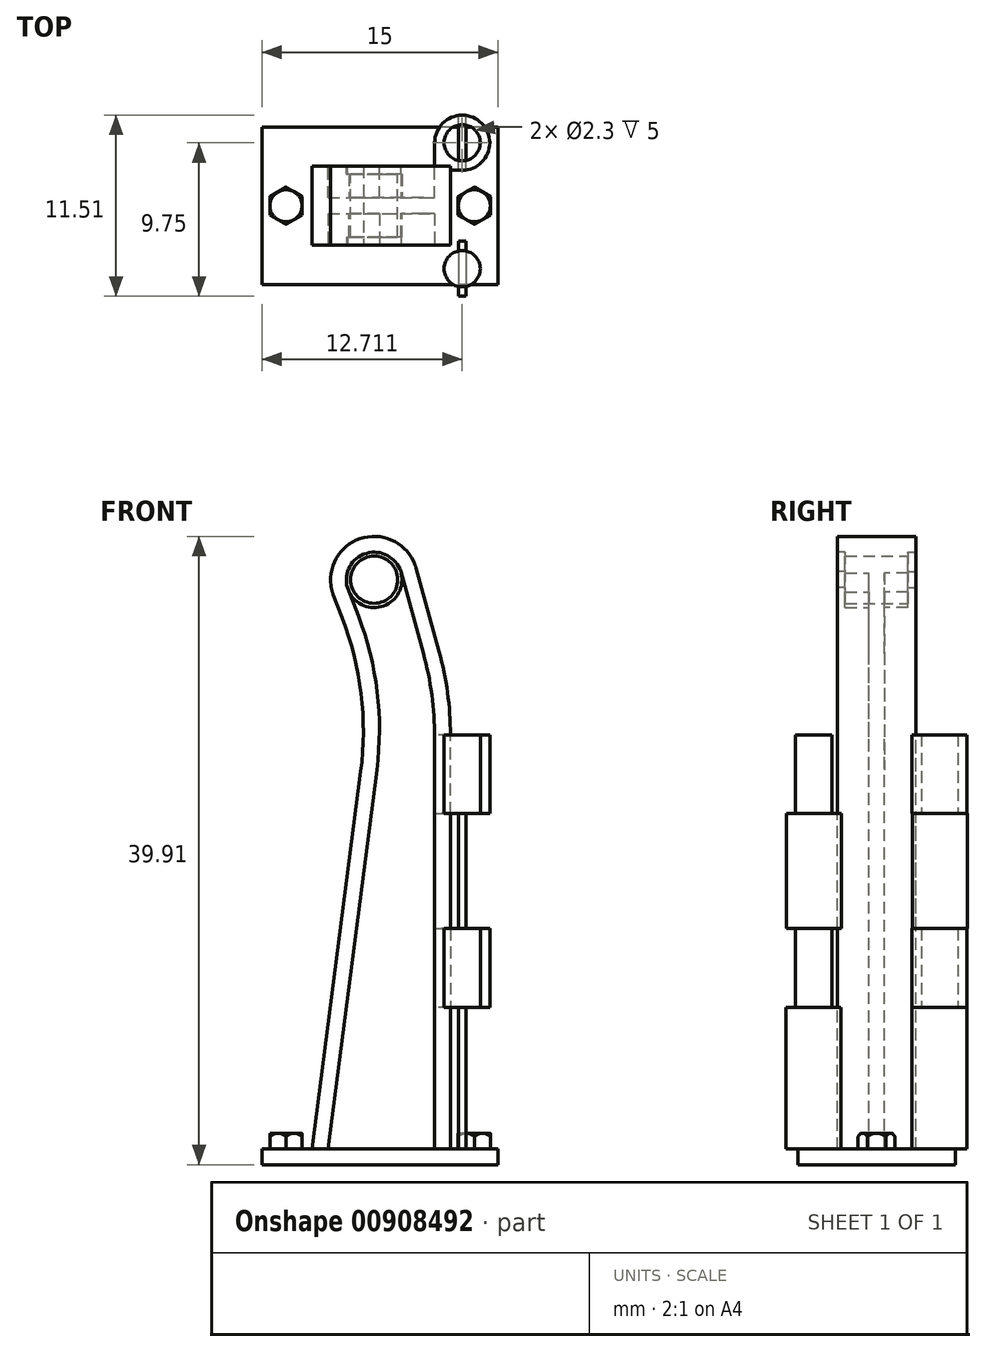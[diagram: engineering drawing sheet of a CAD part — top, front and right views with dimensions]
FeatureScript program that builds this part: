
annotation { "Feature Type Name" : "Feature", "Feature Type Description" : "" }
export const myFeature = defineFeature(function(context is Context, id is Id, definition is map)
    precondition{}
    {
        {
            var Q0;
            Q0=qCreatedBy(makeId("Front.planeOp"),FACE);
            var sketch = newSketch(context, id + "F0", { "sketchPlane" : qUnion([Q0])});
            skLineSegment(sketch, "E0.bottom", {"start": v(-10.54, 39.86) * mm, "end": v(4.46, 40) * mm, "construction": true});
            skLineSegment(sketch, "E0.left", {"start": v(-10.54, 39.86) * mm, "end": v(-10.54, 0) * mm, "construction": true});
            skLineSegment(sketch, "E0.right", {"start": v(4.46, 40) * mm, "end": v(4.46, 0) * mm, "construction": true});
            skLineSegment(sketch, "E1", {"start": v(4.46, 0) * mm, "end": v(4.46, 30) * mm});
            skLineSegment(sketch, "E2", {"start": v(-4.46, 0) * mm, "end": v(-0.58, 30) * mm});
            skLineSegment(sketch, "E3", {"start": v(-0.58, 30) * mm, "end": v(-3.03, 36.33) * mm});
            skLineSegment(sketch, "E4", {"start": v(4.46, 30) * mm, "end": v(2.27, 37.94) * mm});
            skArc(sketch, "E5", {"start": v(2.27, 37.94) * mm, "mid": v(-1.18, 39.79) * mm, "end": v(-3.03, 36.33) * mm});
            skLineSegment(sketch, "E6", {"start": v(-4.46, 0) * mm, "end": v(4.46, 0) * mm});
            skSolve(sketch);
        }
        {
            var Q0;
            Q0=makeQuery(id+"F0.imprint","IMPRINT",FACE,{"disambiguationData":[TD([[makeQuery(id+"F0.imprint","IMPRINT",EDGE,{"derivedFrom":sQuery(id+"F0.wireOp",EDGE,"E1")}),1.0]])]});
            extrude(context, id + "F1", {"entities" : qUnion([Q0]), "endBound" : BoundingType.SYMMETRIC, "depth" : 5 * mm, "offsetDistance" : 25 * mm});
        }
        {
            var Q0;
            Q0=makeQuery(id+"F1.opExtrude","SWEPT_EDGE",EDGE,{"disambiguationData":[OSD([sQuery(id+"F0.wireOp",EDGE,"E1"),sQuery(id+"F0.wireOp",EDGE,"E4")])]});
            var Q1;
            Q1=makeQuery(id+"F1.opExtrude","SWEPT_EDGE",EDGE,{"disambiguationData":[OSD([sQuery(id+"F0.wireOp",EDGE,"E2"),sQuery(id+"F0.wireOp",EDGE,"E3")])]});
            fillet(context, id + "F2", {"entities" : qUnion([Q0, Q1]), "radius" : 20 * mm, "tangentPropagation" : true, "allowEdgeOverflow" : false});
        }
        {
            var Q0;
            Q0=makeQuery(id+"F1.opExtrude","SWEPT_EDGE",EDGE,{"disambiguationData":[OSD([sQuery(id+"F0.wireOp",EDGE,"E3"),sQuery(id+"F0.wireOp",EDGE,"E5")])]});
            var Q1;
            {var subQ0=sQuery(id+"F0.wireOp",EDGE,"E3");Q1=makeQuery(id+"F2.opFillet","BLEND_EDGE",EDGE,{"blendedFrom":[makeQuery(id+"F1.opExtrude","SWEPT_EDGE",EDGE,{"disambiguationData":[OSD([sQuery(id+"F0.wireOp",EDGE,"E2"),subQ0])]}),makeQuery(id+"F1.opExtrude","SWEPT_FACE",FACE,{"disambiguationData":[OSD([subQ0])]})],"blendedInto":[makeQuery(id+"F1.opExtrude","SWEPT_FACE",FACE,{"disambiguationData":[OSD([subQ0])]})]});}
            var Q2;
            Q2=makeQuery(id+"F1.opExtrude","SWEPT_EDGE",EDGE,{"disambiguationData":[OSD([sQuery(id+"F0.wireOp",EDGE,"E4"),sQuery(id+"F0.wireOp",EDGE,"E5")])]});
            fillet(context, id + "F3", {"entities" : qUnion([Q0, Q1, Q2]), "radius" : 2.5 * mm, "tangentPropagation" : true, "allowEdgeOverflow" : false});
        }
        {
            var Q0;
            Q0=makeQuery(id+"F1.opExtrude","CAP_FACE",FACE,{"disambiguationData":[OSD([sQuery(id+"F0.wireOp",EDGE,"E1"),sQuery(id+"F0.wireOp",EDGE,"E2"),sQuery(id+"F0.wireOp",EDGE,"E3"),sQuery(id+"F0.wireOp",EDGE,"E4"),sQuery(id+"F0.wireOp",EDGE,"E5"),sQuery(id+"F0.wireOp",EDGE,"E6")])],"isStart":false});
            var sketch = newSketch(context, id + "F4", { "sketchPlane" : qUnion([Q0])});
            skLineSegment(sketch, "E7.0", {"start": v(3.46, 1) * mm, "end": v(3.46, 29.86) * mm});
            skArc(sketch, "E7.1", {"start": v(1.31, 37.66) * mm, "mid": v(-0.88, 38.83) * mm, "end": v(-2.08, 36.66) * mm});
            skLineSegment(sketch, "E7.2", {"start": v(0.44, 30.12) * mm, "end": v(-2.08, 36.66) * mm});
            skLineSegment(sketch, "E7.3", {"start": v(3.46, 29.86) * mm, "end": v(1.31, 37.66) * mm});
            skLineSegment(sketch, "E7.4", {"start": v(-3.32, 1) * mm, "end": v(0.44, 30.12) * mm});
            skLineSegment(sketch, "E7.5", {"start": v(-3.32, 1) * mm, "end": v(3.46, 1) * mm});
            skLineSegment(sketch, "E8", {"start": v(-0.38, 37.14) * mm, "end": v(-0.38, 38.32) * mm, "construction": true});
            skSolve(sketch);
        }
        {
            var Q0;
            Q0=makeQuery(id+"F4.imprint","IMPRINT",FACE,{"disambiguationData":[TD([[makeQuery(id+"F4.imprint","IMPRINT",EDGE,{"derivedFrom":sQuery(id+"F4.wireOp",EDGE,"E7.0")}),1.0]])]});
            extrude(context, id + "F5", {"entities" : qUnion([Q0]), "operationType" : NewBodyOperationType.REMOVE, "oppositeDirection" : true, "depth" : 2 * mm, "offsetDistance" : 25 * mm});
        }
        {
            var Q0;
            Q0=makeQuery(id+"F5.boolean.opBoolean","COPY",EDGE,{"derivedFrom":makeQuery(id+"F5.opExtrude","SWEPT_EDGE",EDGE,{"disambiguationData":[OSD([sQuery(id+"F4.wireOp",EDGE,"E7.2"),sQuery(id+"F4.wireOp",EDGE,"E7.4")])]})});
            var Q1;
            Q1=makeQuery(id+"F5.boolean.opBoolean","COPY",EDGE,{"derivedFrom":makeQuery(id+"F5.opExtrude","SWEPT_EDGE",EDGE,{"disambiguationData":[OSD([sQuery(id+"F4.wireOp",EDGE,"E7.0"),sQuery(id+"F4.wireOp",EDGE,"E7.3")])]})});
            fillet(context, id + "F6", {"entities" : qUnion([Q0, Q1]), "radius" : 20 * mm, "tangentPropagation" : true, "allowEdgeOverflow" : false});
        }
        {
            var Q0;
            Q0=makeQuery(id+"F1.opExtrude","CAP_FACE",FACE,{"disambiguationData":[OSD([sQuery(id+"F0.wireOp",EDGE,"E1"),sQuery(id+"F0.wireOp",EDGE,"E2"),sQuery(id+"F0.wireOp",EDGE,"E3"),sQuery(id+"F0.wireOp",EDGE,"E4"),sQuery(id+"F0.wireOp",EDGE,"E5"),sQuery(id+"F0.wireOp",EDGE,"E6")])],"isStart":true});
            var sketch = newSketch(context, id + "F7", { "sketchPlane" : qUnion([Q0])});
            skLineSegment(sketch, "E9.MirrorCS", {"start": v(-3.46, 1) * mm, "end": v(-3.46, 29.86) * mm});
            skLineSegment(sketch, "E10.MirrorCS", {"start": v(-3.46, 29.86) * mm, "end": v(-1.31, 37.66) * mm});
            skArc(sketch, "E11.MirrorCS", {"start": v(-1.31, 37.66) * mm, "mid": v(0.88, 38.83) * mm, "end": v(2.08, 36.66) * mm});
            skLineSegment(sketch, "E12.MirrorCS", {"start": v(3.32, 1) * mm, "end": v(-3.46, 1) * mm});
            skLineSegment(sketch, "E13.MirrorCS", {"start": v(3.32, 1) * mm, "end": v(-0.44, 30.12) * mm});
            skLineSegment(sketch, "E14.MirrorCS", {"start": v(-0.44, 30.12) * mm, "end": v(2.08, 36.66) * mm});
            skSolve(sketch);
        }
        {
            var Q0;
            Q0=makeQuery(id+"F7.imprint","IMPRINT",FACE,{"disambiguationData":[TD([[makeQuery(id+"F7.imprint","IMPRINT",EDGE,{"derivedFrom":sQuery(id+"F7.wireOp",EDGE,"E9.MirrorCS")}),-1.0]])]});
            extrude(context, id + "F8", {"entities" : qUnion([Q0]), "operationType" : NewBodyOperationType.REMOVE, "oppositeDirection" : true, "depth" : 2 * mm, "offsetDistance" : 25 * mm});
        }
        {
            var Q0;
            Q0=qCreatedBy(makeId("Top.planeOp"),FACE);
            var sketch = newSketch(context, id + "F9", { "sketchPlane" : qUnion([Q0])});
            skLineSegment(sketch, "E15.bottom", {"start": v(7.5, -5) * mm, "end": v(-7.5, -5) * mm});
            skLineSegment(sketch, "E15.top", {"start": v(7.5, 5) * mm, "end": v(-7.5, 5) * mm});
            skLineSegment(sketch, "E15.left", {"start": v(7.5, -5) * mm, "end": v(7.5, 5) * mm});
            skLineSegment(sketch, "E15.right", {"start": v(-7.5, -5) * mm, "end": v(-7.5, 5) * mm});
            skPoint(sketch, "E15.middle", {"position": v(0, 0) * mm});
            skLineSegment(sketch, "E16", {"start": v(-16.24, 0) * mm, "end": v(12.47, 0) * mm, "construction": true});
            skLineSegment(sketch, "E17", {"start": v(-5.98, 1.97) * mm, "end": v(-5.98, -1.97) * mm, "construction": true});
            skLineSegment(sketch, "E18.MirrorCS", {"start": v(5.98, 1.97) * mm, "end": v(5.98, -1.97) * mm, "construction": true});
            skPoint(sketch, "E19", {"position": v(-5.98, 0) * mm});
            skPoint(sketch, "E20", {"position": v(5.98, 0) * mm});
            skSolve(sketch);
        }
        {
            var Q0;
            Q0=makeQuery(id+"F9.imprint","IMPRINT",FACE,{"disambiguationData":[TD([[makeQuery(id+"F9.imprint","IMPRINT",EDGE,{"derivedFrom":sQuery(id+"F9.wireOp",EDGE,"E15.bottom")}),-1.0]])]});
            extrude(context, id + "F10", {"entities" : qUnion([Q0]), "operationType" : NewBodyOperationType.ADD, "depth" : 1 * mm, "offsetDistance" : 25 * mm});
        }
        {
            var Q0;
            Q0=qCreatedBy(makeId("Top.planeOp"),FACE);
            cPlane(context, id + "F11", {"entities" : qUnion([Q0]), "cplaneType" : CPlaneType.OFFSET, "offset" : 10 * mm, "width" : 150 * mm, "height" : 150 * mm});
        }
        {
            var Q0;
            Q0=makeQuery(id+"F8.boolean.opBoolean","COPY",EDGE,{"derivedFrom":makeQuery(id+"F8.opExtrude","SWEPT_EDGE",EDGE,{"disambiguationData":[OSD([sQuery(id+"F7.wireOp",EDGE,"E13.MirrorCS"),sQuery(id+"F7.wireOp",EDGE,"E14.MirrorCS")])]})});
            var Q1;
            Q1=makeQuery(id+"F8.boolean.opBoolean","COPY",EDGE,{"derivedFrom":makeQuery(id+"F8.opExtrude","SWEPT_EDGE",EDGE,{"disambiguationData":[OSD([sQuery(id+"F7.wireOp",EDGE,"E9.MirrorCS"),sQuery(id+"F7.wireOp",EDGE,"E10.MirrorCS")])]})});
            fillet(context, id + "F12", {"entities" : qUnion([Q0, Q1]), "radius" : 20 * mm, "tangentPropagation" : true, "allowEdgeOverflow" : false});
        }
        {
            var Q0;
            Q0=qCreatedBy(id+"F11.planeOp",FACE);
            var sketch = newSketch(context, id + "F13", { "sketchPlane" : qUnion([Q0])});
            skArc(sketch, "E21", {"start": v(5.21, 2.25) * mm, "mid": v(6.45, 5.24) * mm, "end": v(3.46, 4) * mm});
            skLineSegment(sketch, "E22", {"start": v(5.21, 2.5) * mm, "end": v(5.21, 5.48) * mm, "construction": true});
            skCircle(sketch, "E23", {"center": v(5.21, 4) * mm, "radius": 1.15 * mm});
            skLineSegment(sketch, "E24", {"start": v(3.46, 4) * mm, "end": v(3.46, 2.25) * mm});
            skLineSegment(sketch, "E25", {"start": v(3.46, 2.25) * mm, "end": v(5.21, 2.25) * mm});
            skCircle(sketch, "E26.MirrorC", {"center": v(5.21, -4) * mm, "radius": 1.15 * mm});
            skLineSegment(sketch, "E27.MirrorCS", {"start": v(5.21, -2.5) * mm, "end": v(5.21, -5.48) * mm, "construction": true});
            skLineSegment(sketch, "E28", {"start": v(6, -0.4) * mm, "end": v(8.23, -0.4) * mm, "construction": true});
            skPoint(sketch, "E29.orphan", {"position": v(3.46, 2.5) * mm});
            skLineSegment(sketch, "E30", {"start": v(5.96, 0) * mm, "end": v(10.84, 0) * mm, "construction": true});
            skArc(sketch, "E31.MirrorCS", {"start": v(5.21, -2.25) * mm, "mid": v(6.45, -5.24) * mm, "end": v(3.46, -4) * mm});
            skLineSegment(sketch, "E32.MirrorCS", {"start": v(3.46, -4) * mm, "end": v(3.46, -2.25) * mm});
            skLineSegment(sketch, "E33.MirrorCS", {"start": v(3.46, -2.25) * mm, "end": v(5.21, -2.25) * mm});
            skSolve(sketch);
        }
        {
            var Q0;
            Q0=makeQuery(id+"F13.imprint","IMPRINT",FACE,{"disambiguationData":[TD([[makeQuery(id+"F13.imprint","IMPRINT",EDGE,{"derivedFrom":sQuery(id+"F13.wireOp",EDGE,"E26.MirrorC")}),1.0]])]});
            var Q1;
            Q1=makeQuery(id+"F13.imprint","IMPRINT",FACE,{"disambiguationData":[TD([[makeQuery(id+"F13.imprint","IMPRINT",EDGE,{"derivedFrom":sQuery(id+"F13.wireOp",EDGE,"E21")}),1.0]])]});
            extrude(context, id + "F14", {"entities" : qUnion([Q0, Q1]), "operationType" : NewBodyOperationType.ADD, "depth" : 17.3 * mm, "offsetDistance" : 25 * mm});
        }
        {
            var Q0;
            Q0=qCreatedBy(makeId("Right.planeOp"),FACE);
            cPlane(context, id + "F15", {"entities" : qUnion([Q0]), "cplaneType" : CPlaneType.OFFSET, "offset" : 8 * mm, "width" : 150 * mm, "height" : 150 * mm});
        }
        {
            var Q0;
            Q0=qCreatedBy(id+"F15.planeOp",FACE);
            var sketch = newSketch(context, id + "F16", { "sketchPlane" : qUnion([Q0])});
            skLineSegment(sketch, "E34", {"start": v(-2.5, 32.3) * mm, "end": v(-2.5, 27.3) * mm, "construction": true});
            skLineSegment(sketch, "E35", {"start": v(-2.5, 5) * mm, "end": v(-2.5, 0) * mm, "construction": true});
            skLineSegment(sketch, "E36.top", {"start": v(-2.5, 5) * mm, "end": v(-6.5, 5) * mm, "construction": true});
            skLineSegment(sketch, "E36.left", {"start": v(-2.5, 10) * mm, "end": v(-2.5, 5) * mm, "construction": true});
            skLineSegment(sketch, "E36.right", {"start": v(-6.5, 10) * mm, "end": v(-6.5, 5) * mm, "construction": true});
            skLineSegment(sketch, "E37", {"start": v(-2.5, 10) * mm, "end": v(-2.5, 27.3) * mm, "construction": true});
            skLineSegment(sketch, "E38.bottom", {"start": v(-6.5, 27.3) * mm, "end": v(-2.5, 27.3) * mm, "construction": true});
            skLineSegment(sketch, "E38.top", {"start": v(-6.5, 22.3) * mm, "end": v(-2.5, 22.3) * mm, "construction": true});
            skLineSegment(sketch, "E38.left", {"start": v(-6.5, 27.3) * mm, "end": v(-6.5, 22.3) * mm, "construction": true});
            skLineSegment(sketch, "E38.right", {"start": v(-2.5, 27.3) * mm, "end": v(-2.5, 22.3) * mm, "construction": true});
            skLineSegment(sketch, "E39.bottom", {"start": v(-6.5, 15) * mm, "end": v(-2.5, 15) * mm, "construction": true});
            skLineSegment(sketch, "E39.top", {"start": v(-6.5, 10) * mm, "end": v(-2.5, 10) * mm, "construction": true});
            skLineSegment(sketch, "E39.left", {"start": v(-6.5, 15) * mm, "end": v(-6.5, 10) * mm, "construction": true});
            skLineSegment(sketch, "E39.right", {"start": v(-2.5, 15) * mm, "end": v(-2.5, 10) * mm, "construction": true});
            skLineSegment(sketch, "E40.bottom", {"start": v(-6.5, 22.3) * mm, "end": v(-2.5, 22.3) * mm});
            skLineSegment(sketch, "E40.top", {"start": v(-6.5, 15) * mm, "end": v(-2.5, 15) * mm});
            skLineSegment(sketch, "E40.left", {"start": v(-6.5, 22.3) * mm, "end": v(-6.5, 15) * mm});
            skLineSegment(sketch, "E40.right", {"start": v(-2.5, 22.3) * mm, "end": v(-2.5, 15) * mm});
            skLineSegment(sketch, "E41", {"start": v(0, 0) * mm, "end": v(0, 7.16) * mm, "construction": true});
            skLineSegment(sketch, "E42.MirrorCS", {"start": v(2.5, 22.3) * mm, "end": v(2.5, 15) * mm});
            skLineSegment(sketch, "E43.MirrorCS", {"start": v(6.5, 15) * mm, "end": v(2.5, 15) * mm});
            skLineSegment(sketch, "E44.MirrorCS", {"start": v(2.5, 15) * mm, "end": v(2.5, 10) * mm, "construction": true});
            skLineSegment(sketch, "E45.MirrorCS", {"start": v(2.5, 27.3) * mm, "end": v(2.5, 22.3) * mm, "construction": true});
            skLineSegment(sketch, "E46.MirrorCS", {"start": v(6.5, 22.3) * mm, "end": v(2.5, 22.3) * mm});
            skLineSegment(sketch, "E47.MirrorCS", {"start": v(6.5, 15) * mm, "end": v(2.5, 15) * mm, "construction": true});
            skLineSegment(sketch, "E48.MirrorCS", {"start": v(2.5, 5) * mm, "end": v(2.5, 0) * mm, "construction": true});
            skLineSegment(sketch, "E49.MirrorCS", {"start": v(6.5, 22.3) * mm, "end": v(2.5, 22.3) * mm, "construction": true});
            skLineSegment(sketch, "E50.MirrorCS", {"start": v(2.5, 10) * mm, "end": v(2.5, 27.3) * mm, "construction": true});
            skLineSegment(sketch, "E51.MirrorCS", {"start": v(6.5, 27.3) * mm, "end": v(6.5, 22.3) * mm, "construction": true});
            skLineSegment(sketch, "E52.MirrorCS", {"start": v(6.5, 10) * mm, "end": v(2.5, 10) * mm, "construction": true});
            skLineSegment(sketch, "E53.MirrorCS", {"start": v(2.5, 10) * mm, "end": v(2.5, 5) * mm, "construction": true});
            skLineSegment(sketch, "E54.MirrorCS", {"start": v(2.5, 5) * mm, "end": v(6.5, 5) * mm, "construction": true});
            skLineSegment(sketch, "E55.MirrorCS", {"start": v(6.5, 15) * mm, "end": v(6.5, 10) * mm, "construction": true});
            skLineSegment(sketch, "E56.MirrorCS", {"start": v(6.5, 27.3) * mm, "end": v(2.5, 27.3) * mm, "construction": true});
            skLineSegment(sketch, "E57.MirrorCS", {"start": v(6.5, 22.3) * mm, "end": v(6.5, 15) * mm});
            skLineSegment(sketch, "E58.MirrorCS", {"start": v(6.5, 10) * mm, "end": v(6.5, 5) * mm, "construction": true});
            skSolve(sketch);
        }
        {
            var Q0;
            Q0 = qSketchRegion(id + "F16", true);
            extrude(context, id + "F17", {"entities" : qUnion([Q0]), "operationType" : NewBodyOperationType.REMOVE, "oppositeDirection" : true, "depth" : 25 * mm, "offsetDistance" : 25 * mm});
        }
        {
            var Q0;
            Q0=makeQuery(id+"F8.boolean.opBoolean","COPY",FACE,{"derivedFrom":makeQuery(id+"F8.opExtrude","CAP_FACE",FACE,{"disambiguationData":[OSD([sQuery(id+"F7.wireOp",EDGE,"E9.MirrorCS"),sQuery(id+"F7.wireOp",EDGE,"E10.MirrorCS"),sQuery(id+"F7.wireOp",EDGE,"E11.MirrorCS"),sQuery(id+"F7.wireOp",EDGE,"E12.MirrorCS"),sQuery(id+"F7.wireOp",EDGE,"E13.MirrorCS"),sQuery(id+"F7.wireOp",EDGE,"E14.MirrorCS")])],"isStart":false})});
            var sketch = newSketch(context, id + "F18", { "sketchPlane" : qUnion([Q0])});
            skLineSegment(sketch, "E59", {"start": v(-1.31, 37.66) * mm, "end": v(2.08, 36.66) * mm, "construction": true});
            skPoint(sketch, "E60", {"position": v(0.38, 37.16) * mm});
            skLineSegment(sketch, "E61", {"start": v(0.38, 37.16) * mm, "end": v(0.27, 36.79) * mm, "construction": true});
            skArc(sketch, "E62", {"start": v(-1.05, 37.58) * mm, "mid": v(-0.04, 35.72) * mm, "end": v(1.82, 36.73) * mm, "construction": true});
            skSolve(sketch);
        }
        {
            var Q0;
            Q0=sQuery(id+"F18.wireOp",VERTEX,"E60");
            var Q1;
            Q1=makeQuery(id+"F1.opExtrude","SWEPT_BODY",BODY,{"disambiguationData":[OSD([sQuery(id+"F0.wireOp",EDGE,"E1"),sQuery(id+"F0.wireOp",EDGE,"E2"),sQuery(id+"F0.wireOp",EDGE,"E3"),sQuery(id+"F0.wireOp",EDGE,"E4"),sQuery(id+"F0.wireOp",EDGE,"E5"),sQuery(id+"F0.wireOp",EDGE,"E6")])]});
            hole(context, id + "F19", {"style" : HoleStyle.SIMPLE, "endStyle" : HoleEndStyle.BLIND, "holeDiameter" : 3 * mm, "majorDiameter" : 5 * mm, "holeDepth" : 5 * mm, "isTappedThrough" : true, "tappedDepth" : 12 * mm, "tapClearance" : 3, "startFromSketch" : true, "locations" : qUnion([Q0]), "scope" : qUnion([Q1])});
        }
        {
            var Q0;
            Q0=qCreatedBy(makeId("Front.planeOp"),FACE);
            var sketch = newSketch(context, id + "F20", { "sketchPlane" : qUnion([Q0])});
            skLineSegment(sketch, "E63", {"start": v(-1.82, 36.73) * mm, "end": v(1.05, 37.58) * mm, "construction": true});
            skCircle(sketch, "E64.converted", {"center": v(-0.38, 37.16) * mm, "radius": 1.5 * mm});
            skLineSegment(sketch, "E65", {"start": v(-2.08, 36.66) * mm, "end": v(-3.07, 36.36) * mm, "construction": true});
            skLineSegment(sketch, "E66", {"start": v(2.52, 38.02) * mm, "end": v(1.31, 37.66) * mm, "construction": true});
            skCircle(sketch, "E67", {"center": v(-0.38, 37.16) * mm, "radius": 1.77 * mm});
            skSolve(sketch);
        }
        {
            var Q0;
            Q0 = qSketchRegion(id + "F20", true);
            extrude(context, id + "F21", {"entities" : qUnion([Q0]), "operationType" : NewBodyOperationType.ADD, "depth" : 2 * mm, "offsetDistance" : 25 * mm});
        }
        {
            var Q0;
            Q0=qCreatedBy(makeId("Front.planeOp"),FACE);
            var sketch = newSketch(context, id + "F22", { "sketchPlane" : qUnion([Q0])});
            skLineSegment(sketch, "E68", {"start": v(4.46, 30.73) * mm, "end": v(4.46, 27.3) * mm, "construction": true});
            skLineSegment(sketch, "E69", {"start": v(4.46, 10) * mm, "end": v(4.46, 6.93) * mm, "construction": true});
            skLineSegment(sketch, "E70.bottom", {"start": v(4.46, 27.3) * mm, "end": v(8.46, 27.3) * mm, "construction": true});
            skLineSegment(sketch, "E70.top", {"start": v(4.46, 22.3) * mm, "end": v(8.46, 22.3) * mm, "construction": true});
            skLineSegment(sketch, "E70.left", {"start": v(4.46, 27.3) * mm, "end": v(4.46, 22.3) * mm, "construction": true});
            skLineSegment(sketch, "E70.right", {"start": v(8.46, 27.3) * mm, "end": v(8.46, 22.3) * mm, "construction": true});
            skLineSegment(sketch, "E71.bottom", {"start": v(4.46, 15) * mm, "end": v(8.46, 15) * mm, "construction": true});
            skLineSegment(sketch, "E71.top", {"start": v(4.46, 10) * mm, "end": v(8.46, 10) * mm, "construction": true});
            skLineSegment(sketch, "E71.left", {"start": v(4.46, 15) * mm, "end": v(4.46, 10) * mm, "construction": true});
            skLineSegment(sketch, "E71.right", {"start": v(8.46, 15) * mm, "end": v(8.46, 10) * mm, "construction": true});
            skLineSegment(sketch, "E72.bottom", {"start": v(4.46, 22.3) * mm, "end": v(8.46, 22.3) * mm});
            skLineSegment(sketch, "E72.top", {"start": v(4.46, 15) * mm, "end": v(8.46, 15) * mm});
            skLineSegment(sketch, "E72.left", {"start": v(4.46, 22.3) * mm, "end": v(4.46, 15) * mm});
            skLineSegment(sketch, "E72.right", {"start": v(8.46, 22.3) * mm, "end": v(8.46, 15) * mm});
            skSolve(sketch);
        }
        {
            var Q0;
            Q0 = qSketchRegion(id + "F22", true);
            extrude(context, id + "F23", {"entities" : qUnion([Q0]), "operationType" : NewBodyOperationType.REMOVE, "endBound" : BoundingType.SYMMETRIC, "depth" : 25 * mm, "offsetDistance" : 25 * mm});
        }
        {
            var Q0;
            Q0 = qSketchRegion(id + "F20", true);
            extrude(context, id + "F24", {"entities" : qUnion([Q0]), "operationType" : NewBodyOperationType.ADD, "oppositeDirection" : true, "depth" : 2 * mm, "offsetDistance" : 25 * mm});
        }
        {
            var Q0;
            Q0=makeQuery(id+"F10.boolean.opBoolean","MERGE",FACE,{"derivedFrom":[makeQuery(id+"F5.boolean.opBoolean","COPY",FACE,{"derivedFrom":makeQuery(id+"F5.opExtrude","SWEPT_FACE",FACE,{"disambiguationData":[OSD([sQuery(id+"F4.wireOp",EDGE,"E7.5")])]})}),makeQuery(id+"F8.boolean.opBoolean","COPY",FACE,{"derivedFrom":makeQuery(id+"F8.opExtrude","SWEPT_FACE",FACE,{"disambiguationData":[OSD([sQuery(id+"F7.wireOp",EDGE,"E12.MirrorCS")])]})}),makeQuery(id+"F10.opExtrude","CAP_FACE",FACE,{"disambiguationData":[OSD([sQuery(id+"F9.wireOp",EDGE,"E15.bottom"),sQuery(id+"F9.wireOp",EDGE,"E15.top"),sQuery(id+"F9.wireOp",EDGE,"E15.left"),sQuery(id+"F9.wireOp",EDGE,"E15.right")])],"isStart":false})]});
            var sketch = newSketch(context, id + "F25", { "sketchPlane" : qUnion([Q0])});
            skLineSegment(sketch, "E73", {"start": v(0, 0) * mm, "end": v(0, -7.2) * mm, "construction": true});
            skPoint(sketch, "E73.endSnap0", {"position": v(0, -5) * mm});
            skLineSegment(sketch, "E74", {"start": v(16.07, 0) * mm, "end": v(5.98, 0) * mm, "construction": true});
            skCircle(sketch, "E75.cCircle", {"center": v(5.98, 0) * mm, "radius": 1.02 * mm, "construction": true});
            skLineSegment(sketch, "E75.0", {"start": v(7, 0.59) * mm, "end": v(7, -0.59) * mm});
            skLineSegment(sketch, "E75.1", {"start": v(7, -0.59) * mm, "end": v(5.98, -1.18) * mm});
            skLineSegment(sketch, "E75.2", {"start": v(5.98, -1.18) * mm, "end": v(4.96, -0.59) * mm});
            skLineSegment(sketch, "E75.3", {"start": v(4.96, -0.59) * mm, "end": v(4.96, 0.59) * mm});
            skLineSegment(sketch, "E75.4", {"start": v(4.96, 0.59) * mm, "end": v(5.98, 1.18) * mm});
            skLineSegment(sketch, "E75.5", {"start": v(5.98, 1.18) * mm, "end": v(7, 0.59) * mm});
            skPoint(sketch, "E75.0.midPoint", {"position": v(7, 0) * mm});
            skLineSegment(sketch, "E76.MirrorCS", {"start": v(-4.96, -0.59) * mm, "end": v(-4.96, 0.59) * mm});
            skLineSegment(sketch, "E77.MirrorCS", {"start": v(-5.98, -1.18) * mm, "end": v(-4.96, -0.59) * mm});
            skLineSegment(sketch, "E78.MirrorCS", {"start": v(-7, 0.59) * mm, "end": v(-7, -0.59) * mm});
            skLineSegment(sketch, "E79.MirrorCS", {"start": v(-7, -0.59) * mm, "end": v(-5.98, -1.18) * mm});
            skCircle(sketch, "E80.MirrorC", {"center": v(-5.98, 0) * mm, "radius": 1.02 * mm, "construction": true});
            skLineSegment(sketch, "E81.MirrorCS", {"start": v(-4.96, 0.59) * mm, "end": v(-5.98, 1.18) * mm});
            skPoint(sketch, "E82.MirrorP", {"position": v(-7, 0) * mm});
            skLineSegment(sketch, "E83.MirrorCS", {"start": v(-5.98, 1.18) * mm, "end": v(-7, 0.59) * mm});
            skSolve(sketch);
        }
        {
            var Q0;
            Q0 = qSketchRegion(id + "F25", true);
            extrude(context, id + "F26", {"entities" : qUnion([Q0]), "operationType" : NewBodyOperationType.ADD, "depth" : 1 * mm, "offsetDistance" : 25 * mm});
        }
        {
            var Q0;
            Q0=qCreatedBy(makeId("Front.planeOp"),FACE);
            var sketch = newSketch(context, id + "F27", { "sketchPlane" : qUnion([Q0])});
            skLineSegment(sketch, "E84", {"start": v(7, 2) * mm, "end": v(7.32, 2) * mm});
            skLineSegment(sketch, "E85", {"start": v(7.32, 2) * mm, "end": v(7.32, 1.55) * mm});
            skLineSegment(sketch, "E86", {"start": v(7.32, 1.55) * mm, "end": v(7, 2) * mm});
            skLineSegment(sketch, "E87", {"start": v(5.98, 0) * mm, "end": v(10.61, 0) * mm, "construction": true});
            skLineSegment(sketch, "E88", {"start": v(5.98, 0) * mm, "end": v(5.98, 2.56) * mm, "construction": true});
            skLineSegment(sketch, "E89", {"start": v(0, 0) * mm, "end": v(0, 5.41) * mm, "construction": true});
            skLineSegment(sketch, "E90.MirrorCS", {"start": v(-7.32, 1.55) * mm, "end": v(-7, 2) * mm});
            skLineSegment(sketch, "E91.MirrorCS", {"start": v(-7, 2) * mm, "end": v(-7.32, 2) * mm});
            skLineSegment(sketch, "E92.MirrorCS", {"start": v(-7.32, 2) * mm, "end": v(-7.32, 1.55) * mm});
            skLineSegment(sketch, "E93.MirrorCS", {"start": v(-5.98, 0) * mm, "end": v(-10.61, 0) * mm, "construction": true});
            skLineSegment(sketch, "E94.MirrorCS", {"start": v(-5.98, 0) * mm, "end": v(-5.98, 2.56) * mm, "construction": true});
            skSolve(sketch);
        }
        {
            var Q0;
            Q0=makeQuery(id+"F27.imprint","IMPRINT",FACE,{"disambiguationData":[TD([[makeQuery(id+"F27.imprint","IMPRINT",EDGE,{"derivedFrom":sQuery(id+"F27.wireOp",EDGE,"E84")}),-1.0]])]});
            var Q1;
            Q1=sQuery(id+"F27.wireOp",EDGE,"E88");
            revolve(context, id + "F28", {"operationType" : NewBodyOperationType.REMOVE, "surfaceOperationType" : NewSurfaceOperationType.NEW, "entities" : qUnion([Q0]), "axis" : qUnion([Q1]), "revolveType" : RevolveType.FULL});
        }
        {
            var Q0;
            Q0=makeQuery(id+"F27.imprint","IMPRINT",FACE,{"disambiguationData":[TD([[makeQuery(id+"F27.imprint","IMPRINT",EDGE,{"derivedFrom":sQuery(id+"F27.wireOp",EDGE,"E90.MirrorCS")}),1.0]])]});
            var Q1;
            Q1=sQuery(id+"F27.wireOp",EDGE,"E94.MirrorCS");
            revolve(context, id + "F29", {"operationType" : NewBodyOperationType.REMOVE, "surfaceOperationType" : NewSurfaceOperationType.NEW, "entities" : qUnion([Q0]), "axis" : qUnion([Q1]), "revolveType" : RevolveType.FULL, "oppositeDirection" : true});
        }
        {
            var Q0;
            Q0=qCreatedBy(id+"F11.planeOp",FACE);
            var sketch = newSketch(context, id + "F30", { "sketchPlane" : qUnion([Q0])});
            skLineSegment(sketch, "E95.bottom", {"start": v(5.46, 2.25) * mm, "end": v(4.96, 2.25) * mm});
            skLineSegment(sketch, "E95.top", {"start": v(5.46, 5.75) * mm, "end": v(4.96, 5.75) * mm});
            skLineSegment(sketch, "E95.left", {"start": v(5.46, 2.25) * mm, "end": v(5.46, 5.75) * mm});
            skLineSegment(sketch, "E95.right", {"start": v(4.96, 2.25) * mm, "end": v(4.96, 5.75) * mm});
            skPoint(sketch, "E95.middle", {"position": v(5.21, 4) * mm});
            skLineSegment(sketch, "E96", {"start": v(0, 0) * mm, "end": v(3.44, 0) * mm, "construction": true});
            skLineSegment(sketch, "E97.MirrorCS", {"start": v(5.46, -2.25) * mm, "end": v(4.96, -2.25) * mm});
            skPoint(sketch, "E98.MirrorP", {"position": v(5.21, -4) * mm});
            skLineSegment(sketch, "E99.MirrorCS", {"start": v(5.46, -5.75) * mm, "end": v(4.96, -5.75) * mm});
            skLineSegment(sketch, "E100.MirrorCS", {"start": v(5.46, -2.25) * mm, "end": v(5.46, -5.75) * mm});
            skLineSegment(sketch, "E101.MirrorCS", {"start": v(4.96, -2.25) * mm, "end": v(4.96, -5.75) * mm});
            skSolve(sketch);
        }
        {
            var Q0;
            {var subQ5=sQuery(id+"F30.wireOp",EDGE,"2gFtqV93-Ntm6-dRez-hQgn-FwB0Ine7L3JD.right");Q0=makeQuery(id+"F30.imprint","IMPRINT",FACE,{"disambiguationData":[TD([[makeQuery(id+"F30.imprint","IMPRINT",EDGE,{"derivedFrom":subQ5}),-1.0]])]});}
            var Q1;
            {var subQ5=sQuery(id+"F30.wireOp",EDGE,"2gFtqV93-Ntm6-dRez-hQgn-FwB0Ine7L3JD.left");Q1=makeQuery(id+"F30.imprint","IMPRINT",FACE,{"disambiguationData":[TD([[makeQuery(id+"F30.imprint","IMPRINT",EDGE,{"derivedFrom":subQ5}),1.0]])]});}
            var Q2;
            {var subQ0=sQuery(id+"F30.wireOp",EDGE,"2gFtqV93-Ntm6-dRez-hQgn-FwB0Ine7L3JD.bottom");var subQ1=sQuery(id+"F30.wireOp",EDGE,"E95.left");var subQ2=makeQuery(id+"F30.imprint","INTERSECT",VERTEX,{"derivedFrom":[subQ1,subQ0]});Q2=makeQuery(id+"F30.imprint","IMPRINT",FACE,{"disambiguationData":[TD([[makeQuery(id+"F30.imprint","IMPRINT",EDGE,{"disambiguationData":[TD([[subQ2,-1.0]])],"derivedFrom":subQ1}),1.0]])]});}
            var Q3;
            {var subQ0=sQuery(id+"F30.wireOp",EDGE,"E95.top");Q3=makeQuery(id+"F30.imprint","IMPRINT",FACE,{"disambiguationData":[TD([[makeQuery(id+"F30.imprint","IMPRINT",EDGE,{"derivedFrom":subQ0}),1.0]])]});}
            var Q4;
            {var subQ0=sQuery(id+"F30.wireOp",EDGE,"E95.bottom");Q4=makeQuery(id+"F30.imprint","IMPRINT",FACE,{"disambiguationData":[TD([[makeQuery(id+"F30.imprint","IMPRINT",EDGE,{"derivedFrom":subQ0}),-1.0]])]});}
            var Q5;
            {var subQ0=sQuery(id+"F30.wireOp",EDGE,"E99.MirrorCS");Q5=makeQuery(id+"F30.imprint","IMPRINT",FACE,{"disambiguationData":[TD([[makeQuery(id+"F30.imprint","IMPRINT",EDGE,{"derivedFrom":subQ0}),-1.0]])]});}
            var Q6;
            {var subQ0=sQuery(id+"F30.wireOp",EDGE,"E97.MirrorCS");Q6=makeQuery(id+"F30.imprint","IMPRINT",FACE,{"disambiguationData":[TD([[makeQuery(id+"F30.imprint","IMPRINT",EDGE,{"derivedFrom":subQ0}),1.0]])]});}
            var Q7;
            {var subQ0=sQuery(id+"F30.wireOp",EDGE,"271807a9-6e93-4d3d-bef6-e0091bf9e4bb9.MirrorCS");var subQ1=sQuery(id+"F30.wireOp",EDGE,"E100.MirrorCS");var subQ2=makeQuery(id+"F30.imprint","INTERSECT",VERTEX,{"derivedFrom":[subQ1,subQ0]});Q7=makeQuery(id+"F30.imprint","IMPRINT",FACE,{"disambiguationData":[TD([[makeQuery(id+"F30.imprint","IMPRINT",EDGE,{"disambiguationData":[TD([[subQ2,-1.0]])],"derivedFrom":subQ1}),-1.0]])]});}
            var Q8;
            {var subQ0=sQuery(id+"F30.wireOp",EDGE,"271807a9-6e93-4d3d-bef6-e0091bf9e4bb4.MirrorCS");Q8=makeQuery(id+"F30.imprint","IMPRINT",FACE,{"disambiguationData":[TD([[makeQuery(id+"F30.imprint","IMPRINT",EDGE,{"derivedFrom":subQ0}),-1.0]])]});}
            var Q9;
            {var subQ0=sQuery(id+"F30.wireOp",EDGE,"271807a9-6e93-4d3d-bef6-e0091bf9e4bb3.MirrorCS");Q9=makeQuery(id+"F30.imprint","IMPRINT",FACE,{"disambiguationData":[TD([[makeQuery(id+"F30.imprint","IMPRINT",EDGE,{"derivedFrom":subQ0}),1.0]])]});}
            var Q10;
            Q10=makeQuery(id+"F10.boolean.opBoolean","MERGE",FACE,{"derivedFrom":[makeQuery(id+"F5.boolean.opBoolean","COPY",FACE,{"derivedFrom":makeQuery(id+"F5.opExtrude","SWEPT_FACE",FACE,{"disambiguationData":[OSD([sQuery(id+"F4.wireOp",EDGE,"E7.5")])]})}),makeQuery(id+"F8.boolean.opBoolean","COPY",FACE,{"derivedFrom":makeQuery(id+"F8.opExtrude","SWEPT_FACE",FACE,{"disambiguationData":[OSD([sQuery(id+"F7.wireOp",EDGE,"E12.MirrorCS")])]})}),makeQuery(id+"F10.opExtrude","CAP_FACE",FACE,{"disambiguationData":[OSD([sQuery(id+"F9.wireOp",EDGE,"E15.bottom"),sQuery(id+"F9.wireOp",EDGE,"E15.top"),sQuery(id+"F9.wireOp",EDGE,"E15.left"),sQuery(id+"F9.wireOp",EDGE,"E15.right")])],"isStart":false})]});
            extrude(context, id + "F31", {"entities" : qUnion([Q0, Q1, Q2, Q3, Q4, Q5, Q6, Q7, Q8, Q9]), "endBound" : BoundingType.UP_TO_SURFACE, "oppositeDirection" : true, "depth" : 25 * mm, "endBoundEntityFace" : qUnion([Q10]), "offsetDistance" : 25 * mm});
        }
        {
            var Q0;
            Q0=makeQuery(id+"F23.boolean.opBoolean","MERGE",FACE,{"derivedFrom":[makeQuery(id+"F17.boolean.opBoolean","COPY",FACE,{"derivedFrom":makeQuery(id+"F17.opExtrude","SWEPT_FACE",FACE,{"disambiguationData":[OSD([sQuery(id+"F16.wireOp",EDGE,"E40.top")])]})})],"fromTools":[makeQuery(id+"F23.opExtrude","SWEPT_FACE",FACE,{"disambiguationData":[OSD([sQuery(id+"F22.wireOp",EDGE,"E72.top")])]})]});
            var sketch = newSketch(context, id + "F32", { "sketchPlane" : qUnion([Q0])});
            skPoint(sketch, "E102", {"position": v(5.21, -3.99) * mm});
            skLineSegment(sketch, "E103.bottom", {"start": v(5.46, 2.26) * mm, "end": v(4.96, 2.26) * mm});
            skLineSegment(sketch, "E103.top", {"start": v(5.46, 5.76) * mm, "end": v(4.96, 5.76) * mm});
            skLineSegment(sketch, "E103.left", {"start": v(5.46, 2.26) * mm, "end": v(5.46, 5.76) * mm});
            skLineSegment(sketch, "E103.right", {"start": v(4.96, 2.26) * mm, "end": v(4.96, 5.76) * mm});
            skPoint(sketch, "E103.middle", {"position": v(5.21, 4.01) * mm});
            skLineSegment(sketch, "E104", {"start": v(-0.15, 0.01) * mm, "end": v(3.29, 0.01) * mm, "construction": true});
            skLineSegment(sketch, "E105.MirrorCS", {"start": v(5.46, -2.24) * mm, "end": v(4.96, -2.24) * mm});
            skLineSegment(sketch, "E106.MirrorCS", {"start": v(5.46, -5.74) * mm, "end": v(4.96, -5.74) * mm});
            skLineSegment(sketch, "E107.MirrorCS", {"start": v(5.46, -2.24) * mm, "end": v(5.46, -4.24) * mm});
            skLineSegment(sketch, "E108.MirrorCS", {"start": v(4.96, -2.24) * mm, "end": v(4.96, -4.24) * mm});
            skPoint(sketch, "E109.endSnap0", {"position": v(5.21, -3.74) * mm});
            skLineSegment(sketch, "E110.trimOffspring", {"start": v(4.96, -4.24) * mm, "end": v(4.96, -5.74) * mm});
            skLineSegment(sketch, "E111.trimOffspring", {"start": v(5.46, -4.24) * mm, "end": v(5.46, -5.74) * mm});
            skSolve(sketch);
        }
        {
            var Q0;
            Q0 = qSketchRegion(id + "F32", true);
            var Q1;
            Q1=makeQuery(id+"F23.boolean.opBoolean","MERGE",FACE,{"derivedFrom":[makeQuery(id+"F17.boolean.opBoolean","COPY",FACE,{"derivedFrom":makeQuery(id+"F17.opExtrude","SWEPT_FACE",FACE,{"disambiguationData":[OSD([sQuery(id+"F16.wireOp",EDGE,"E40.bottom")])]})})],"fromTools":[makeQuery(id+"F23.opExtrude","SWEPT_FACE",FACE,{"disambiguationData":[OSD([sQuery(id+"F22.wireOp",EDGE,"E72.bottom")])]})]});
            extrude(context, id + "F33", {"entities" : qUnion([Q0]), "endBound" : BoundingType.UP_TO_SURFACE, "depth" : 25 * mm, "endBoundEntityFace" : qUnion([Q1]), "offsetDistance" : 25 * mm});
        }
    });
